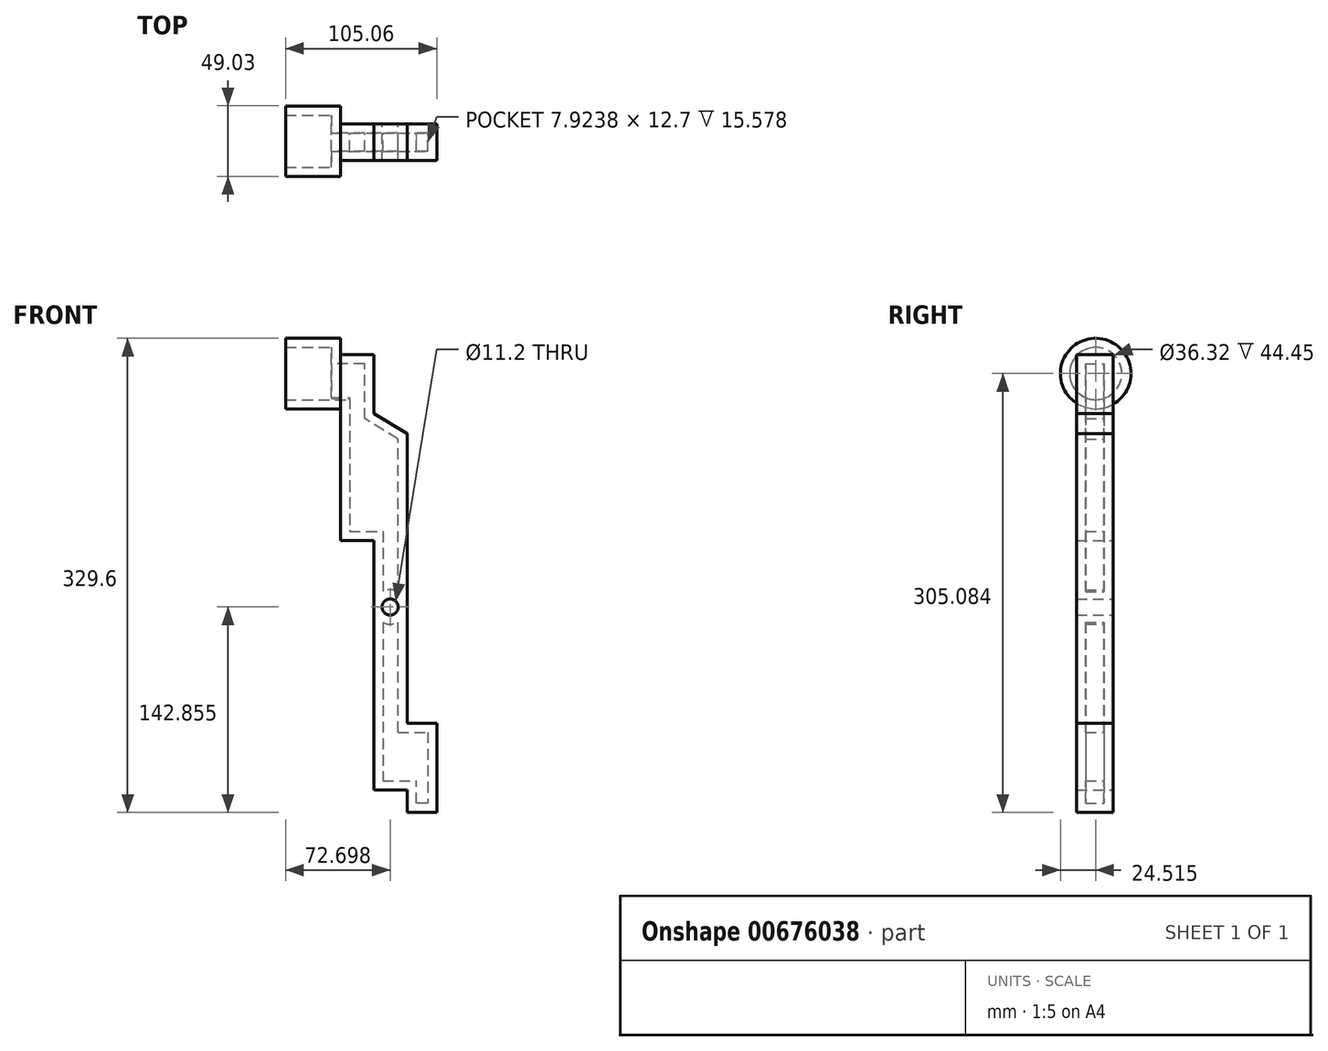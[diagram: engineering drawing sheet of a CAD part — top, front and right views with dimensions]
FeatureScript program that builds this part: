
annotation { "Feature Type Name" : "Feature", "Feature Type Description" : "" }
export const myFeature = defineFeature(function(context is Context, id is Id, definition is map)
    precondition{}
    {
        {
            var Q0;
            Q0=qCreatedBy(makeId("Front.planeOp"),FACE);
            var sketch = newSketch(context, id + "F0", { "sketchPlane" : qUnion([Q0])});
            skLineSegment(sketch, "E0", {"start": v(-53.85, 64.84) * mm, "end": v(-53.85, -119.55) * mm});
            skLineSegment(sketch, "E1", {"start": v(-53.85, -119.55) * mm, "end": v(-30.69, -119.55) * mm});
            skLineSegment(sketch, "E2", {"start": v(-30.69, -119.55) * mm, "end": v(-30.69, 128.1) * mm});
            skLineSegment(sketch, "E3", {"start": v(-30.69, 128.1) * mm, "end": v(-53.85, 142.16) * mm});
            skLineSegment(sketch, "E4", {"start": v(-53.85, 142.16) * mm, "end": v(-53.85, 183.24) * mm});
            skLineSegment(sketch, "E5", {"start": v(-53.85, 183.24) * mm, "end": v(-77.02, 183.24) * mm});
            skLineSegment(sketch, "E6", {"start": v(-77.02, 183.24) * mm, "end": v(-77.02, 53.83) * mm});
            skLineSegment(sketch, "E7", {"start": v(-77.02, 53.83) * mm, "end": v(-53.85, 53.83) * mm});
            skLineSegment(sketch, "E8", {"start": v(-53.85, 142.16) * mm, "end": v(-53.85, 64.84) * mm});
            skLineSegment(sketch, "E9", {"start": v(-30.69, -73) * mm, "end": v(-10.06, -73) * mm});
            skLineSegment(sketch, "E10", {"start": v(-10.06, -73) * mm, "end": v(-10.06, -135.12) * mm});
            skLineSegment(sketch, "E11", {"start": v(-10.06, -135.12) * mm, "end": v(-30.69, -135.12) * mm});
            skLineSegment(sketch, "E12", {"start": v(-30.69, -135.12) * mm, "end": v(-30.69, -119.55) * mm});
            skCircle(sketch, "E13", {"center": v(-42.42, 7.73) * mm, "radius": 5.6 * mm});
            skSolve(sketch);
        }
        {
            var Q0;
            Q0=makeQuery(id+"F0.imprint","IMPRINT",FACE,{"disambiguationData":[TD([[makeQuery(id+"F0.imprint","IMPRINT",EDGE,{"derivedFrom":sQuery(id+"F0.wireOp",EDGE,"E4")}),1.0]])]});
            var Q1;
            {var subQ1=sQuery(id+"F0.wireOp",EDGE,"E1");Q1=makeQuery(id+"F0.imprint","IMPRINT",FACE,{"disambiguationData":[TD([[makeQuery(id+"F0.imprint","IMPRINT",EDGE,{"derivedFrom":subQ1}),1.0]])]});}
            var Q2;
            {var subQ0=sQuery(id+"F0.wireOp",EDGE,"E9");Q2=makeQuery(id+"F0.imprint","IMPRINT",FACE,{"disambiguationData":[TD([[makeQuery(id+"F0.imprint","IMPRINT",EDGE,{"derivedFrom":subQ0}),-1.0]])]});}
            extrude(context, id + "F1", {"entities" : qUnion([Q0, Q1, Q2]), "depth" : 25.4 * mm, "offsetDistance" : 25.4 * mm});
        }
        {
            var Q0;
            Q0=makeQuery(id+"F1.opExtrude","SWEPT_FACE",FACE,{"disambiguationData":[OSD([sQuery(id+"F0.wireOp",EDGE,"E6")])]});
            var sketch = newSketch(context, id + "F2", { "sketchPlane" : qUnion([Q0])});
            skCircle(sketch, "E14", {"center": v(12, 169.96) * mm, "radius": 24.51 * mm});
            skSolve(sketch);
        }
        {
            var Q0;
            {var subQ1=sQuery(id+"F0.wireOp",EDGE,"E6");var subQ6=makeQuery(id+"F1.opExtrude","SWEPT_EDGE",EDGE,{"disambiguationData":[OSD([sQuery(id+"F0.wireOp",EDGE,"E5"),subQ1])]});Q0=makeQuery(id+"F2.imprint","IMPRINT",FACE,{"disambiguationData":[TD([[makeQuery(id+"F2.imprint","IMPRINT",EDGE,{"derivedFrom":subQ6}),-1.0]])]});}
            var Q1;
            {var subQ1=sQuery(id+"F0.wireOp",EDGE,"E6");var subQ6=makeQuery(id+"F1.opExtrude","SWEPT_EDGE",EDGE,{"disambiguationData":[OSD([sQuery(id+"F0.wireOp",EDGE,"E5"),subQ1])]});Q1=makeQuery(id+"F2.imprint","IMPRINT",FACE,{"disambiguationData":[TD([[makeQuery(id+"F2.imprint","IMPRINT",EDGE,{"derivedFrom":subQ6}),1.0]])]});}
            extrude(context, id + "F3", {"entities" : qUnion([Q0, Q1]), "operationType" : NewBodyOperationType.ADD, "depth" : 38.1 * mm, "offsetDistance" : 25.4 * mm});
        }
        {
            var Q0;
            Q0=makeQuery(id+"F3.opExtrude","CAP_FACE",FACE,{"disambiguationData":[OSD([sQuery(id+"F2.wireOp",EDGE,"E14")])],"isStart":false});
            shell(context, id + "F4", {"entities" : qUnion([Q0]), "thickness" : 6.35 * mm});
        }
    });
